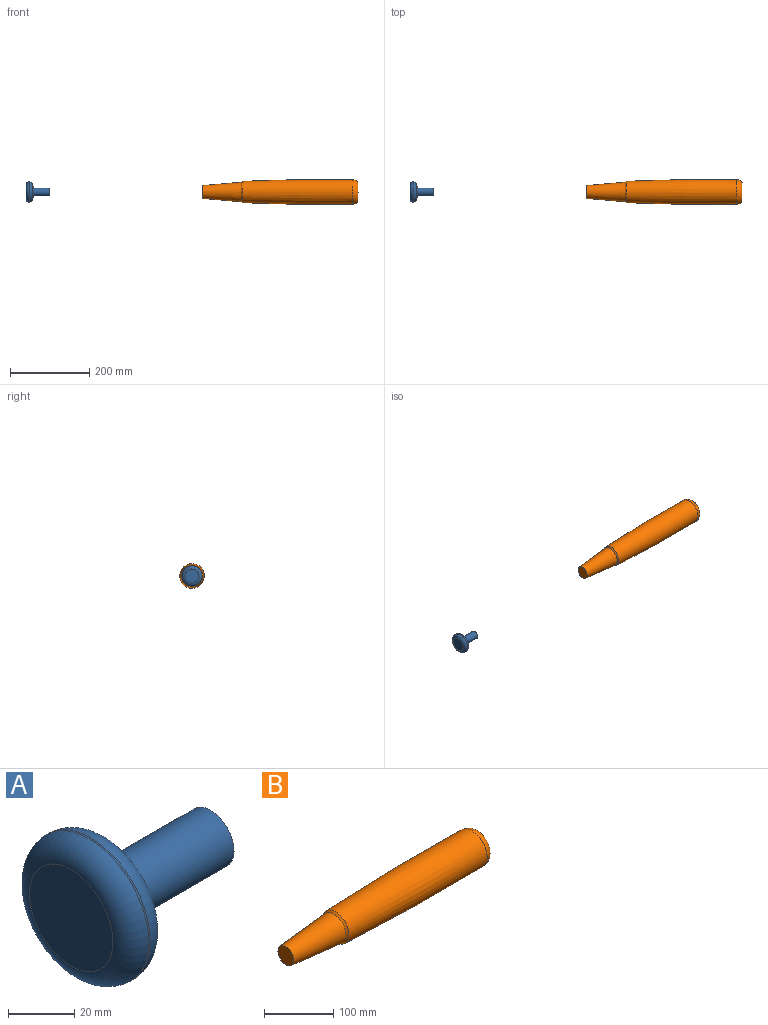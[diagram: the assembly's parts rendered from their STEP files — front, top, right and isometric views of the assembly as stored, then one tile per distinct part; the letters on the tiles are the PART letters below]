
ASSEMBLY  parts=2 mates=2
PART A: 8 faces, bbox 59.4x55x55 mm
  f0: plane 35.56x35.56mm, normal (-1,0,0), area 993.1mm2, adj f6
  f1: cylinder r=25.4mm len=50.8mm, axis (1,0,0), area 101.3mm2, adj f6,f7
  f2: plane 35.56x35.56mm, normal (1,0,0), area 110.3mm2, adj f3,f7
  f3: cone r=9.91mm half-angle=58.6deg, axis (-1,0,0), area 673.4mm2, adj f2,f4
  f4: cylinder r=9.91mm len=39.37mm, axis (1,0,0), area 2450.4mm2, adj f3,f5
  f5: plane 19.81x19.81mm, normal (1,0,0), area 308.3mm2, adj f4
  f6: torus R=17.78mm, axis (1,0,0), area 1702mm2, adj f0,f1
  f7: torus R=17.78mm, axis (-1,0,0), area 1702mm2, adj f1,f2
PART B: 6 faces, bbox 395.1x66.6x66.6 mm
  f0: plane 32.46x32.46mm, normal (-1,0,0), area 827.6mm2, adj f1
  f1: revolved ~98.43x49.12mm, area 12681.8mm2, adj f0,f5
  f2: plane 45.62x45.62mm, normal (1,0,0), area 1634.4mm2, adj f3
  f3: torus R=16.62mm, axis (-1,0,0), area 2775.6mm2, adj f2,f4
  f4: revolved ~279.4x62.4mm, area 53274.8mm2, adj f3,f5
  f5: cone r=27.1mm half-angle=38.7deg, axis (1,0,0), area 659.9mm2, adj f1,f4
PLACE A rot(axis=(0.04,0.03,-1),0deg) t=(116.06,3.08,17.33)mm
PLACE B rot(axis=(0.04,0.03,-1),0deg) t=(501.12,3.08,17.33)mm
MATE slider A.f1 <-> B.f3  axis (1,0,0) through (116.06,3.08,17.33)mm
MATE planar A.f1 <-> B.f3  axis (-1,0,0) through (56.62,3.08,17.33)mm
